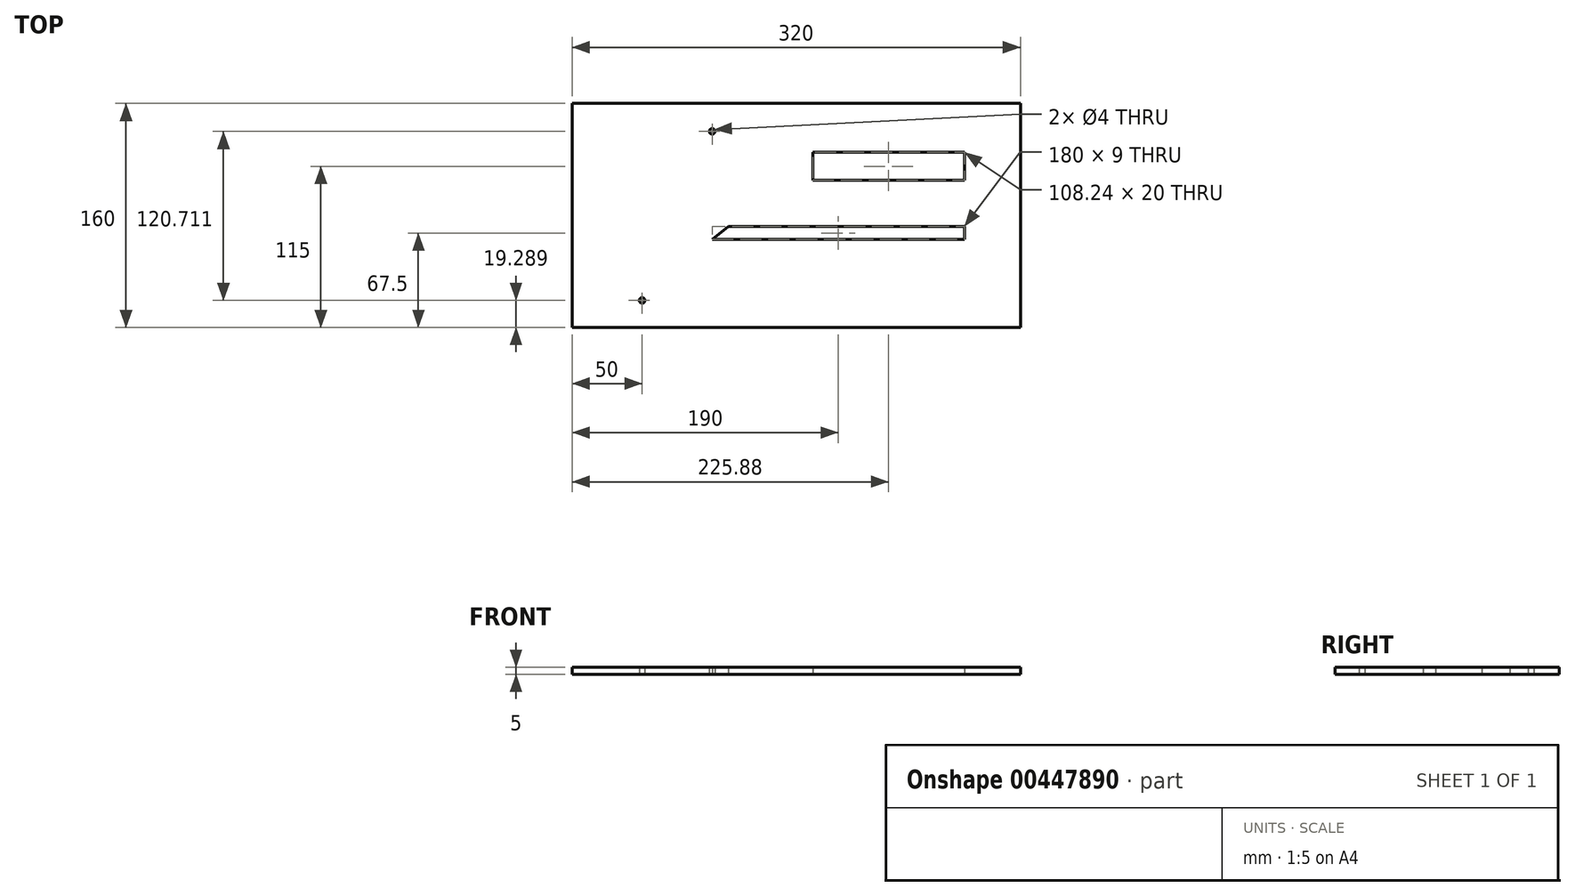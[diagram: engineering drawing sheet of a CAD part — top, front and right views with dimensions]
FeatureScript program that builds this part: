
annotation { "Feature Type Name" : "Feature", "Feature Type Description" : "" }
export const myFeature = defineFeature(function(context is Context, id is Id, definition is map)
    precondition{}
    {
        {
            var Q0;
            Q0=qCreatedBy(makeId("Top.planeOp"),FACE);
            var sketch = newSketch(context, id + "F0", { "sketchPlane" : qUnion([Q0])});
            skLineSegment(sketch, "E0.left", {"start": v(-100, 20) * mm, "end": v(-100, -140) * mm});
            skCircle(sketch, "E1", {"center": v(0, 0) * mm, "radius": 2 * mm});
            skLineSegment(sketch, "E2", {"start": v(-100, -140) * mm, "end": v(220, -140) * mm});
            skPoint(sketch, "E3", {"position": v(71.76, -68) * mm});
            skPoint(sketch, "E4", {"position": v(71.76, -35) * mm});
            skLineSegment(sketch, "E5.left", {"start": v(71.76, -35) * mm, "end": v(71.76, -15) * mm});
            skPoint(sketch, "E6", {"position": v(-50, -120.71) * mm});
            skCircle(sketch, "E7", {"center": v(-50, -120.71) * mm, "radius": 2 * mm});
            skLineSegment(sketch, "E8", {"start": v(0, -77) * mm, "end": v(180, -77) * mm});
            skLineSegment(sketch, "E9", {"start": v(180, -68) * mm, "end": v(180, -77) * mm});
            skPoint(sketch, "E10", {"position": v(11.52, -68) * mm});
            skLineSegment(sketch, "E11", {"start": v(11.52, -68) * mm, "end": v(0, -77) * mm});
            skLineSegment(sketch, "E12", {"start": v(11.52, -68) * mm, "end": v(180, -68) * mm});
            skLineSegment(sketch, "E13", {"start": v(71.76, -35) * mm, "end": v(180, -35) * mm});
            skLineSegment(sketch, "E14", {"start": v(180, -35) * mm, "end": v(180, -15) * mm});
            skLineSegment(sketch, "E15", {"start": v(180, -15) * mm, "end": v(71.76, -15) * mm});
            skLineSegment(sketch, "E16", {"start": v(220, -140) * mm, "end": v(220, 20) * mm});
            skLineSegment(sketch, "E17", {"start": v(-100, 20) * mm, "end": v(220, 20) * mm});
            skSolve(sketch);
        }
        {
            var Q0;
            Q0 = qSketchRegion(id + "F0", true);
            extrude(context, id + "F1", {"entities" : qUnion([Q0]), "depth" : 5 * mm});
        }
    });
